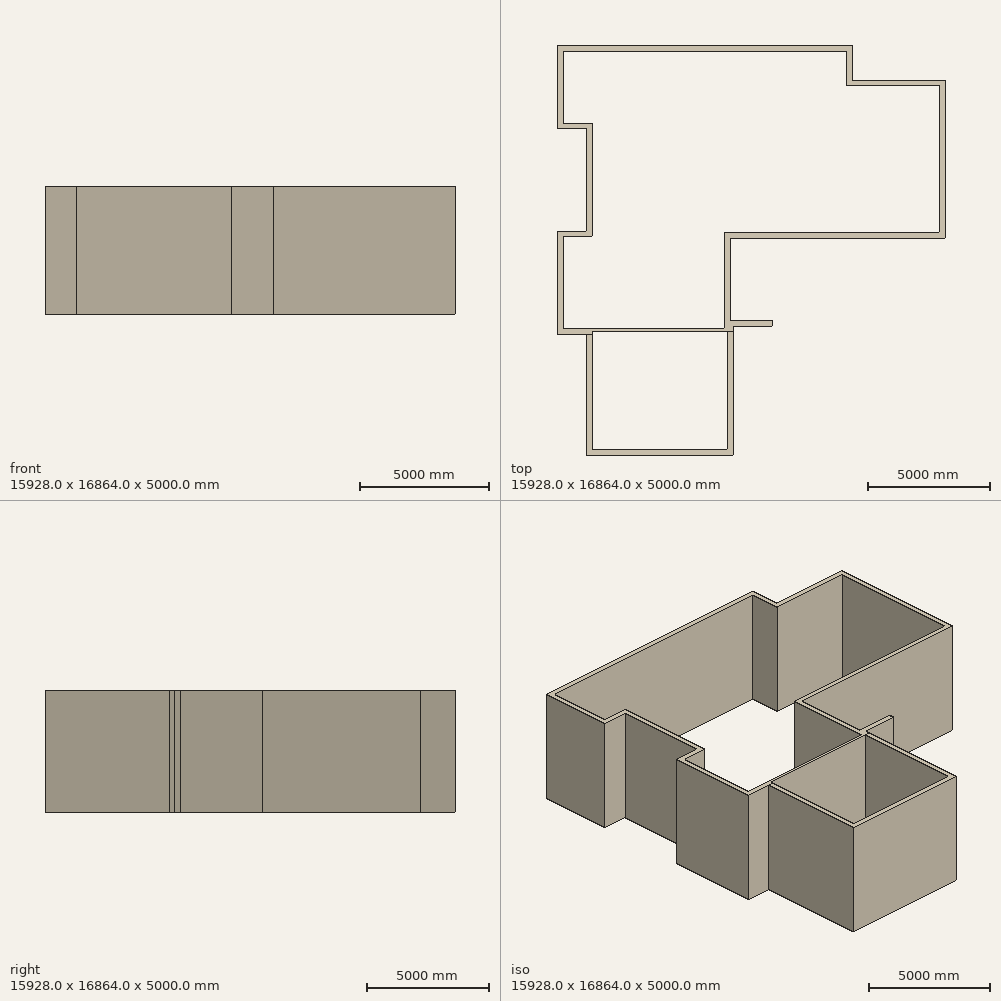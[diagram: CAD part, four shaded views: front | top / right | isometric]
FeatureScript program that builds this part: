
annotation { "Feature Type Name" : "Feature", "Feature Type Description" : "" }
export const myFeature = defineFeature(function(context is Context, id is Id, definition is map)
    precondition{}
    {
        {
            var Q0;
            Q0=qCreatedBy(makeId("Top.planeOp"),FACE);
            var sketch = newSketch(context, id + "F0", { "sketchPlane" : qUnion([Q0])});
            skLineSegment(sketch, "E0", {"start": v(0, 0) * mm, "end": v(0, -4990) * mm});
            skLineSegment(sketch, "E1", {"start": v(0, 0) * mm, "end": v(-1187, 0) * mm});
            skLineSegment(sketch, "E2", {"start": v(-1187, 0) * mm, "end": v(-1187, 4236) * mm});
            skLineSegment(sketch, "E3", {"start": v(-1187, 4236) * mm, "end": v(0, 4236) * mm});
            skLineSegment(sketch, "E4", {"start": v(0, 4236) * mm, "end": v(0, 8442) * mm});
            skLineSegment(sketch, "E5", {"start": v(0, -4990) * mm, "end": v(6030, -4990) * mm});
            skLineSegment(sketch, "E6", {"start": v(6030, -4990) * mm, "end": v(6030, 336) * mm});
            skLineSegment(sketch, "E7", {"start": v(6030, 336) * mm, "end": v(7658, 336) * mm});
            skLineSegment(sketch, "E8", {"start": v(0, 8442) * mm, "end": v(-1187, 8442) * mm});
            skLineSegment(sketch, "E9", {"start": v(-1187, 8442) * mm, "end": v(-1187, 11874) * mm});
            skLineSegment(sketch, "E10", {"start": v(-1187, 11874) * mm, "end": v(10931, 11874) * mm});
            skLineSegment(sketch, "E11", {"start": v(10931, 11874) * mm, "end": v(10931, 10444) * mm});
            skLineSegment(sketch, "E12", {"start": v(10931, 10444) * mm, "end": v(14741, 10444) * mm});
            skLineSegment(sketch, "E13", {"start": v(14741, 10444) * mm, "end": v(14741, 3954) * mm});
            skLineSegment(sketch, "E14", {"start": v(14741, 3954) * mm, "end": v(5915, 3954) * mm});
            skLineSegment(sketch, "E15", {"start": v(7658, 336) * mm, "end": v(7658, 566) * mm});
            skLineSegment(sketch, "E16", {"start": v(7658, 566) * mm, "end": v(5915, 566) * mm});
            skLineSegment(sketch, "E17", {"start": v(5915, 566) * mm, "end": v(5915, 3954) * mm});
            skLineSegment(sketch, "E18.0", {"start": v(5685, 230) * mm, "end": v(5685, 4184) * mm});
            skLineSegment(sketch, "E18.1", {"start": v(14511, 4184) * mm, "end": v(5685, 4184) * mm});
            skLineSegment(sketch, "E18.2", {"start": v(14511, 10214) * mm, "end": v(14511, 4184) * mm});
            skLineSegment(sketch, "E18.3", {"start": v(10701, 10214) * mm, "end": v(14511, 10214) * mm});
            skLineSegment(sketch, "E18.4", {"start": v(10701, 11644) * mm, "end": v(10701, 10214) * mm});
            skLineSegment(sketch, "E18.5", {"start": v(230, 230) * mm, "end": v(-957, 230) * mm});
            skLineSegment(sketch, "E18.6", {"start": v(230, 115) * mm, "end": v(230, -4760) * mm});
            skLineSegment(sketch, "E18.7", {"start": v(230, -4760) * mm, "end": v(5800, -4760) * mm});
            skLineSegment(sketch, "E18.8", {"start": v(5800, -4760) * mm, "end": v(5800, 115) * mm});
            skLineSegment(sketch, "E18.9", {"start": v(-957, 230) * mm, "end": v(-957, 4006) * mm});
            skLineSegment(sketch, "E18.10", {"start": v(-957, 4006) * mm, "end": v(230, 4006) * mm});
            skLineSegment(sketch, "E18.11", {"start": v(230, 4006) * mm, "end": v(230, 8672) * mm});
            skLineSegment(sketch, "E18.12", {"start": v(230, 8672) * mm, "end": v(-957, 8672) * mm});
            skLineSegment(sketch, "E18.13", {"start": v(-957, 8672) * mm, "end": v(-957, 11644) * mm});
            skLineSegment(sketch, "E18.14", {"start": v(-957, 11644) * mm, "end": v(10701, 11644) * mm});
            skLineSegment(sketch, "E19", {"start": v(230, 230) * mm, "end": v(5685, 230) * mm});
            skLineSegment(sketch, "E20", {"start": v(5800, 115) * mm, "end": v(230, 115) * mm});
            skLineSegment(sketch, "E21", {"start": v(5800, 115) * mm, "end": v(6030, 115) * mm});
            skLineSegment(sketch, "E22", {"start": v(0, 0) * mm, "end": v(230, 0) * mm});
            skSolve(sketch);
        }
        {
            var Q0;
            Q0=makeQuery(id+"F0.imprint","IMPRINT",FACE,{"disambiguationData":[TD([[makeQuery(id+"F0.imprint","IMPRINT",EDGE,{"derivedFrom":sQuery(id+"F0.wireOp",EDGE,"E1")}),-1.0]])]});
            extrude(context, id + "F1", {"entities" : qUnion([Q0]), "depth" : 4000 * mm, "offsetDistance" : 25 * mm, "hasSecondDirection" : true, "secondDirectionOppositeDirection" : true, "secondDirectionDepth" : 1000 * mm});
        }
        {
            var Q0;
            Q0=makeQuery(id+"F0.imprint","IMPRINT",FACE,{"disambiguationData":[TD([[makeQuery(id+"F0.imprint","IMPRINT",EDGE,{"derivedFrom":sQuery(id+"F0.wireOp",EDGE,"E0")}),1.0]])]});
            extrude(context, id + "F2", {"entities" : qUnion([Q0]), "depth" : 4000 * mm, "offsetDistance" : 25 * mm, "hasSecondDirection" : true, "secondDirectionOppositeDirection" : true, "secondDirectionDepth" : 1000 * mm});
        }
    });
